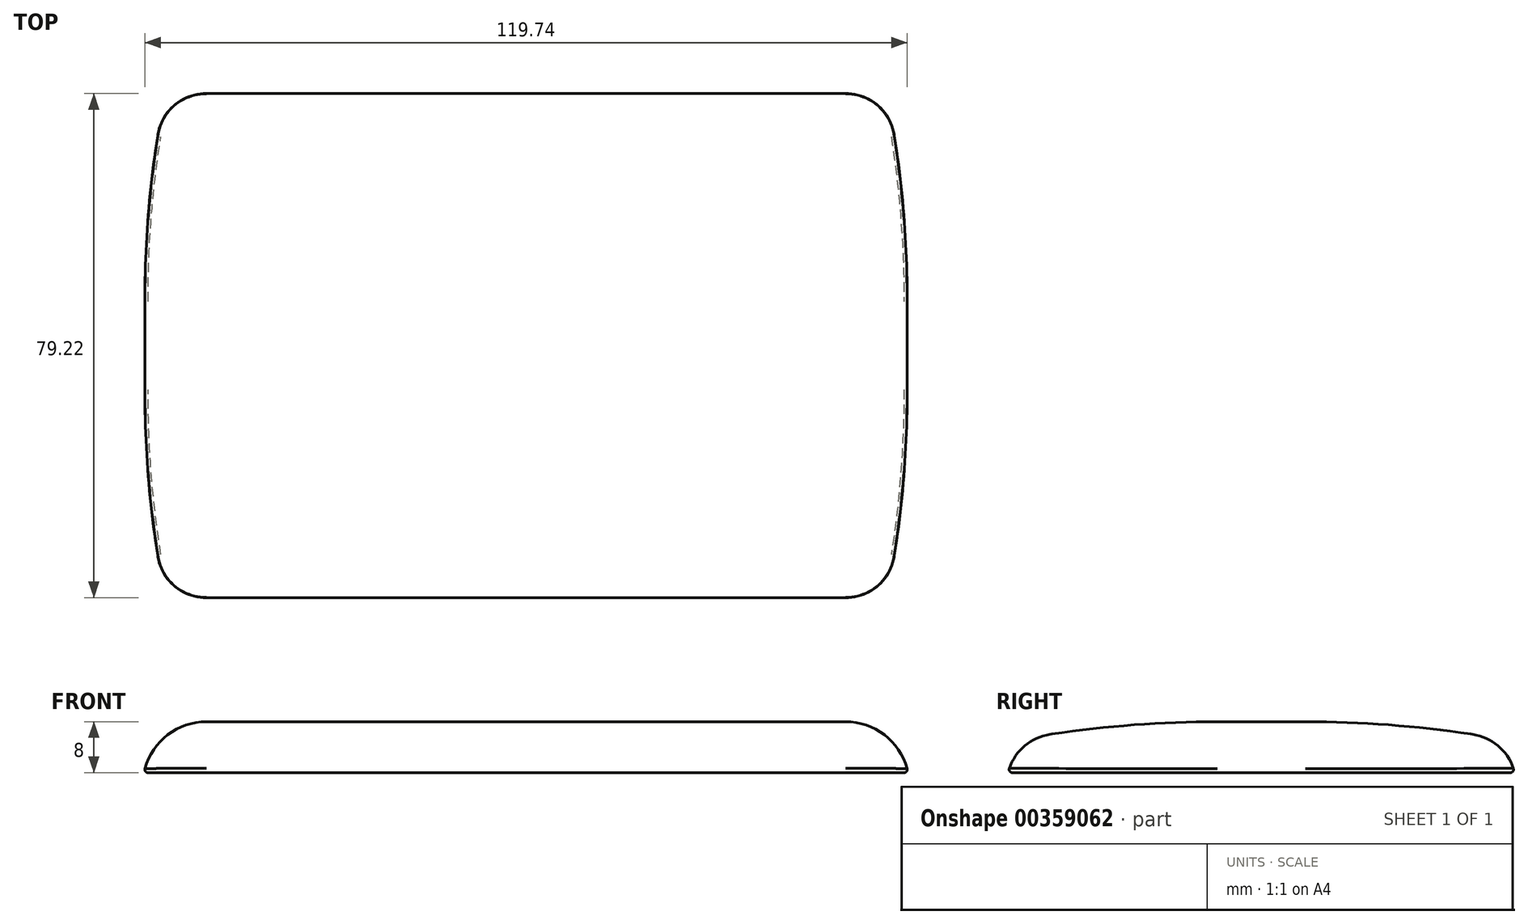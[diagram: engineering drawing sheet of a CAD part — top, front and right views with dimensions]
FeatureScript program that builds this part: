
annotation { "Feature Type Name" : "Feature", "Feature Type Description" : "" }
export const myFeature = defineFeature(function(context is Context, id is Id, definition is map)
    precondition{}
    {
        {
            var Q0;
            Q0=qCreatedBy(makeId("Top.planeOp"),FACE);
            var sketch = newSketch(context, id + "F0", { "sketchPlane" : qUnion([Q0])});
            skLineSegment(sketch, "E0.bottom", {"start": v(60, 40) * mm, "end": v(-60, 40) * mm});
            skLineSegment(sketch, "E0.top", {"start": v(60, -40) * mm, "end": v(-60, -40) * mm});
            skLineSegment(sketch, "E0.left", {"start": v(60, 40) * mm, "end": v(60, -40) * mm});
            skLineSegment(sketch, "E0.right", {"start": v(-60, 40) * mm, "end": v(-60, -40) * mm});
            skPoint(sketch, "E0.middle", {"position": v(0, 0) * mm});
            skSolve(sketch);
        }
        {
            var Q0;
            Q0=makeQuery(id+"F0.imprint","IMPRINT",FACE,{"disambiguationData":[TD([[makeQuery(id+"F0.imprint","IMPRINT",EDGE,{"derivedFrom":sQuery(id+"F0.wireOp",EDGE,"E0.bottom")}),1.0]])]});
            extrude(context, id + "F1", {"entities" : qUnion([Q0]), "depth" : 8 * mm});
        }
        {
            var Q0;
            Q0=makeQuery(id+"F1.opExtrude","CAP_EDGE",EDGE,{"disambiguationData":[OSD([sQuery(id+"F0.wireOp",EDGE,"E0.right")])],"isStart":false});
            var Q1;
            Q1=makeQuery(id+"F1.opExtrude","CAP_EDGE",EDGE,{"disambiguationData":[OSD([sQuery(id+"F0.wireOp",EDGE,"E0.left")])],"isStart":false});
            fillet(context, id + "F2", {"entities" : qUnion([Q0, Q1]), "radius" : 10 * mm, "tangentPropagation" : true, "allowEdgeOverflow" : false});
        }
        {
            var Q0;
            Q0=makeQuery(id+"F1.opExtrude","CAP_EDGE",EDGE,{"disambiguationData":[OSD([sQuery(id+"F0.wireOp",EDGE,"E0.bottom")])],"isStart":false});
            var Q1;
            Q1=makeQuery(id+"F1.opExtrude","CAP_EDGE",EDGE,{"disambiguationData":[OSD([sQuery(id+"F0.wireOp",EDGE,"E0.top")])],"isStart":false});
            chamfer(context, id + "F3", {"entities" : qUnion([Q0, Q1]), "chamferType" : ChamferType.TWO_OFFSETS, "width1" : 20 * mm, "oppositeDirection" : false, "width2" : 3 * mm, "tangentPropagation" : true});
        }
        {
            var Q0;
            {var subQ0=sQuery(id+"F0.wireOp",EDGE,"E0.bottom");Q0=makeQuery(id+"F3.opChamfer","BLEND_EDGE",EDGE,{"blendedFrom":[makeQuery(id+"F1.opExtrude","CAP_EDGE",EDGE,{"disambiguationData":[OSD([subQ0])],"isStart":false}),makeQuery(id+"F1.opExtrude","SWEPT_FACE",FACE,{"disambiguationData":[OSD([subQ0])]})],"blendedInto":[makeQuery(id+"F1.opExtrude","SWEPT_FACE",FACE,{"disambiguationData":[OSD([subQ0])]})]});}
            var Q1;
            {var subQ0=sQuery(id+"F0.wireOp",EDGE,"E0.top");Q1=makeQuery(id+"F3.opChamfer","BLEND_EDGE",EDGE,{"blendedFrom":[makeQuery(id+"F1.opExtrude","CAP_EDGE",EDGE,{"disambiguationData":[OSD([subQ0])],"isStart":false}),makeQuery(id+"F1.opExtrude","SWEPT_FACE",FACE,{"disambiguationData":[OSD([subQ0])]})],"blendedInto":[makeQuery(id+"F1.opExtrude","SWEPT_FACE",FACE,{"disambiguationData":[OSD([subQ0])]})]});}
            fillet(context, id + "F4", {"entities" : qUnion([Q0, Q1]), "radius" : 8 * mm, "tangentPropagation" : true, "allowEdgeOverflow" : false});
        }
        {
            var Q0;
            {var subQ0=sQuery(id+"F0.wireOp",EDGE,"E0.bottom");Q0=makeQuery(id+"F3.opChamfer","BLEND_EDGE",EDGE,{"blendedFrom":[makeQuery(id+"F1.opExtrude","CAP_EDGE",EDGE,{"disambiguationData":[OSD([subQ0])],"isStart":false}),makeQuery(id+"F1.opExtrude","CAP_FACE",FACE,{"disambiguationData":[OSD([subQ0,sQuery(id+"F0.wireOp",EDGE,"E0.top"),sQuery(id+"F0.wireOp",EDGE,"E0.left"),sQuery(id+"F0.wireOp",EDGE,"E0.right")])],"isStart":false})],"blendedInto":[makeQuery(id+"F1.opExtrude","CAP_FACE",FACE,{"disambiguationData":[OSD([subQ0,sQuery(id+"F0.wireOp",EDGE,"E0.top"),sQuery(id+"F0.wireOp",EDGE,"E0.left"),sQuery(id+"F0.wireOp",EDGE,"E0.right")])],"isStart":false})]});}
            var Q1;
            {var subQ0=sQuery(id+"F0.wireOp",EDGE,"E0.top");Q1=makeQuery(id+"F3.opChamfer","BLEND_EDGE",EDGE,{"blendedFrom":[makeQuery(id+"F1.opExtrude","CAP_EDGE",EDGE,{"disambiguationData":[OSD([subQ0])],"isStart":false}),makeQuery(id+"F1.opExtrude","CAP_FACE",FACE,{"disambiguationData":[OSD([sQuery(id+"F0.wireOp",EDGE,"E0.bottom"),subQ0,sQuery(id+"F0.wireOp",EDGE,"E0.left"),sQuery(id+"F0.wireOp",EDGE,"E0.right")])],"isStart":false})],"blendedInto":[makeQuery(id+"F1.opExtrude","CAP_FACE",FACE,{"disambiguationData":[OSD([sQuery(id+"F0.wireOp",EDGE,"E0.bottom"),subQ0,sQuery(id+"F0.wireOp",EDGE,"E0.left"),sQuery(id+"F0.wireOp",EDGE,"E0.right")])],"isStart":false})]});}
            fillet(context, id + "F5", {"entities" : qUnion([Q0, Q1]), "radius" : 175 * mm, "tangentPropagation" : true, "allowEdgeOverflow" : false});
        }
        {
            var Q0;
            Q0=makeQuery(id+"F1.opExtrude","CAP_FACE",FACE,{"disambiguationData":[OSD([sQuery(id+"F0.wireOp",EDGE,"E0.bottom"),sQuery(id+"F0.wireOp",EDGE,"E0.top"),sQuery(id+"F0.wireOp",EDGE,"E0.left"),sQuery(id+"F0.wireOp",EDGE,"E0.right")])],"isStart":true});
            fillet(context, id + "F6", {"entities" : qUnion([Q0]), "radius" : 0.5 * mm, "tangentPropagation" : true, "allowEdgeOverflow" : false});
        }
        {
            var Q0;
            Q0=makeQuery(id+"F1.opExtrude","SWEPT_BODY",BODY,{"disambiguationData":[OSD([sQuery(id+"F0.wireOp",EDGE,"E0.bottom"),sQuery(id+"F0.wireOp",EDGE,"E0.top"),sQuery(id+"F0.wireOp",EDGE,"E0.left"),sQuery(id+"F0.wireOp",EDGE,"E0.right")])]});
            transform(context, id + "F7", {"entities" : qUnion([Q0]), "transformType" : TransformType.TRANSLATION_3D, "dx" : 0 * mm, "dy" : 0 * mm, "dz" : 0 * mm, "makeCopy" : true});
        }
        {
            var Q0;
            Q0=makeQuery(id+"F7.opPattern","COPY",BODY,{"derivedFrom":makeQuery(id+"F1.opExtrude","SWEPT_BODY",BODY,{"disambiguationData":[OSD([sQuery(id+"F0.wireOp",EDGE,"E0.bottom"),sQuery(id+"F0.wireOp",EDGE,"E0.top"),sQuery(id+"F0.wireOp",EDGE,"E0.left"),sQuery(id+"F0.wireOp",EDGE,"E0.right")])]}),"instanceName":"1"});
            deleteBodies(context, id + "F8", {"entities" : qUnion([Q0])});
        }
    });
